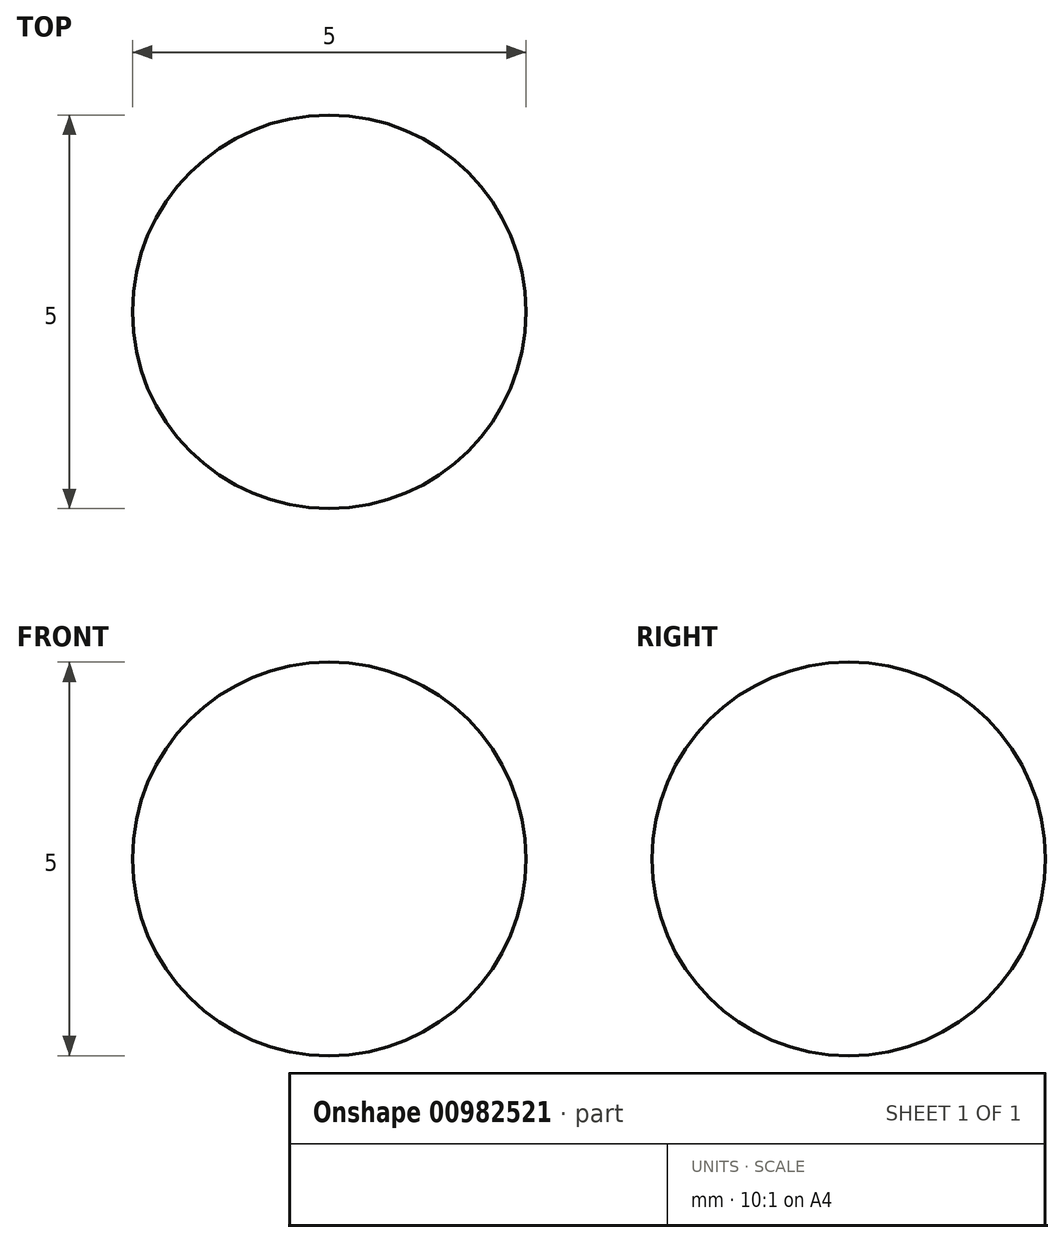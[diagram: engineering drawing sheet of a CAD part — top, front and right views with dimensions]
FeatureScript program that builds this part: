
annotation { "Feature Type Name" : "Feature", "Feature Type Description" : "" }
export const myFeature = defineFeature(function(context is Context, id is Id, definition is map)
    precondition{}
    {
        {
            var Q0;
            Q0=qCreatedBy(makeId("Top.planeOp"),FACE);
            var sketch = newSketch(context, id + "F0", { "sketchPlane" : qUnion([Q0])});
            skLineSegment(sketch, "E0", {"start": v(0, 0) * mm, "end": v(0, 5) * mm, "construction": true});
            skArc(sketch, "E1", {"start": v(0, 5) * mm, "mid": v(-2.5, 2.5) * mm, "end": v(0, 0) * mm});
            skSolve(sketch);
        }
        {
            var Q0;
            Q0=sQuery(id+"F0.wireOp",EDGE,"E0");
            var Q1;
            Q1=sQuery(id+"F0.wireOp",EDGE,"E1");
            var Q2;
            Q2=sQuery(id+"F0.wireOp",EDGE,"E0");
            revolve(context, id + "F1", {"bodyType" : ToolBodyType.SURFACE, "surfaceOperationType" : NewSurfaceOperationType.NEW, "surfaceEntities" : qUnion([Q0, Q1]), "axis" : qUnion([Q2]), "revolveType" : RevolveType.FULL});
        }
    });
